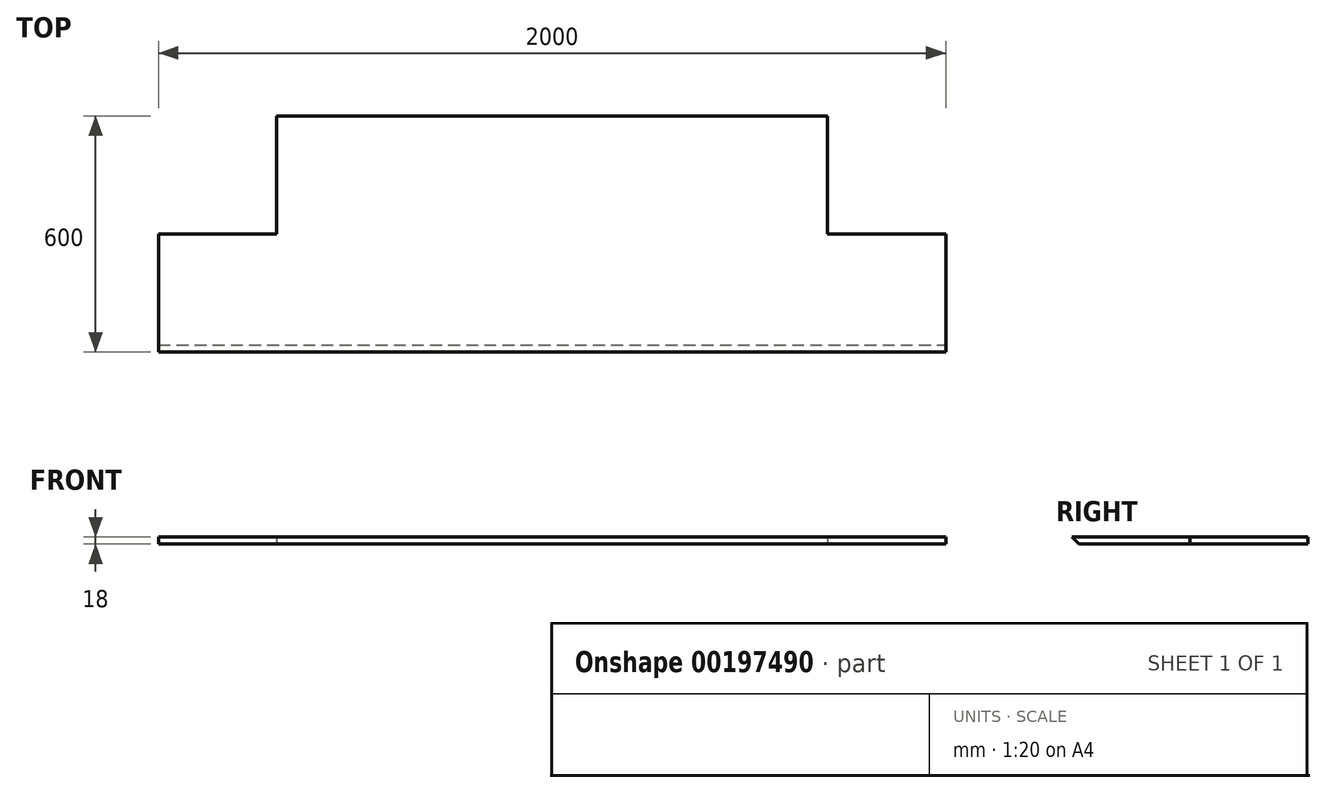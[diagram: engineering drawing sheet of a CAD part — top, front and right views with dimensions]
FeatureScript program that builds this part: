
annotation { "Feature Type Name" : "Feature", "Feature Type Description" : "" }
export const myFeature = defineFeature(function(context is Context, id is Id, definition is map)
    precondition{}
    {
        {
            var Q0;
            Q0=qCreatedBy(makeId("Top.planeOp"),FACE);
            var sketch = newSketch(context, id + "F0", { "sketchPlane" : qUnion([Q0])});
            skLineSegment(sketch, "E0.bottom", {"start": v(1000, 150) * mm, "end": v(700, 150) * mm});
            skLineSegment(sketch, "E0.top", {"start": v(1000, -150) * mm, "end": v(-1000, -150) * mm});
            skLineSegment(sketch, "E0.left", {"start": v(1000, 150) * mm, "end": v(1000, -150) * mm});
            skLineSegment(sketch, "E0.right", {"start": v(-1000, 150) * mm, "end": v(-1000, -150) * mm});
            skPoint(sketch, "E0.middle", {"position": v(0, 0) * mm});
            skLineSegment(sketch, "E1", {"start": v(-700, 150) * mm, "end": v(-700, 450) * mm});
            skLineSegment(sketch, "E2", {"start": v(-700, 450) * mm, "end": v(700, 450) * mm});
            skLineSegment(sketch, "E3", {"start": v(700, 450) * mm, "end": v(700, 150) * mm});
            skLineSegment(sketch, "E4.trimOffspring", {"start": v(-700, 150) * mm, "end": v(-1000, 150) * mm});
            skSolve(sketch);
        }
        {
            var Q0;
            Q0=qSketchRegion(id+"F0",true);
            extrude(context, id + "F1", {"entities" : qUnion([Q0]), "depth" : 18 * mm});
        }
        {
            var Q0;
            Q0=makeQuery(id+"F1.opExtrude","SWEPT_FACE",FACE,{"disambiguationData":[OSD([sQuery(id+"F0.wireOp",EDGE,"E0.left")])]});
            var sketch = newSketch(context, id + "F2", { "sketchPlane" : qUnion([Q0])});
            skLineSegment(sketch, "E5", {"start": v(-150, 18) * mm, "end": v(-132, 0) * mm});
            skLineSegment(sketch, "E6", {"start": v(-132, 0) * mm, "end": v(-150, 0) * mm});
            skLineSegment(sketch, "E7", {"start": v(-150, 0) * mm, "end": v(-150, 18) * mm});
            skSolve(sketch);
        }
        {
            var Q0;
            Q0 = qSketchRegion(id + "F2", true);
            extrude(context, id + "F3", {"entities" : qUnion([Q0]), "operationType" : NewBodyOperationType.REMOVE, "oppositeDirection" : true, "depth" : 2000 * mm});
        }
    });
